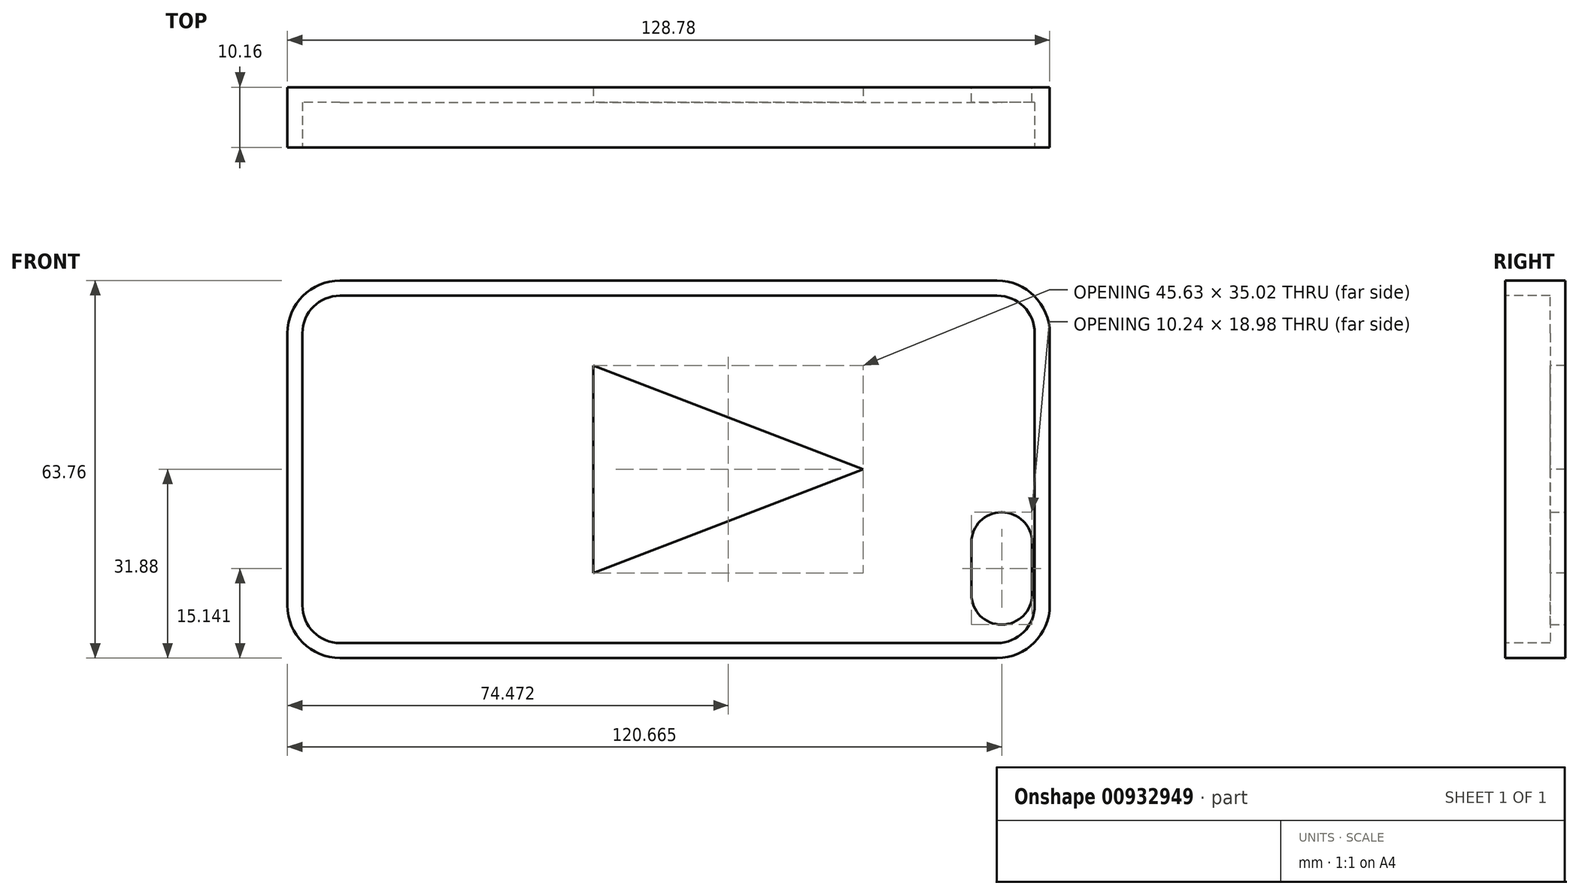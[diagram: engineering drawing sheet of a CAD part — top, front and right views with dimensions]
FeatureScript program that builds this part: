
annotation { "Feature Type Name" : "Feature", "Feature Type Description" : "" }
export const myFeature = defineFeature(function(context is Context, id is Id, definition is map)
    precondition{}
    {
        {
            var Q0;
            Q0=qCreatedBy(makeId("Front.planeOp"),FACE);
            var sketch = newSketch(context, id + "F0", { "sketchPlane" : qUnion([Q0])});
            skLineSegment(sketch, "E0.bottom", {"start": v(-55.5, 31.88) * mm, "end": v(55.5, 31.88) * mm});
            skLineSegment(sketch, "E0.top", {"start": v(-55.5, -31.88) * mm, "end": v(55.5, -31.88) * mm});
            skLineSegment(sketch, "E0.left", {"start": v(-64.39, 22.99) * mm, "end": v(-64.39, -22.99) * mm});
            skLineSegment(sketch, "E0.right", {"start": v(64.39, 22.99) * mm, "end": v(64.39, -22.99) * mm});
            skPoint(sketch, "E0.middle", {"position": v(0, 0) * mm});
            skPoint(sketch, "E1.visualSharp", {"position": v(-64.39, 31.88) * mm});
            skArc(sketch, "E1.filletArc", {"start": v(-55.5, 31.88) * mm, "mid": v(-61.79, 29.27) * mm, "end": v(-64.39, 22.99) * mm});
            skPoint(sketch, "E2.visualSharp", {"position": v(64.39, 31.88) * mm});
            skArc(sketch, "E2.filletArc", {"start": v(64.39, 22.99) * mm, "mid": v(61.79, 29.27) * mm, "end": v(55.5, 31.88) * mm});
            skPoint(sketch, "E3.visualSharp", {"position": v(64.39, -31.88) * mm});
            skArc(sketch, "E3.filletArc", {"start": v(55.5, -31.88) * mm, "mid": v(61.79, -29.27) * mm, "end": v(64.39, -22.99) * mm});
            skPoint(sketch, "E4.visualSharp", {"position": v(-64.39, -31.88) * mm});
            skArc(sketch, "E4.filletArc", {"start": v(-64.39, -22.99) * mm, "mid": v(-61.79, -29.27) * mm, "end": v(-55.5, -31.88) * mm});
            skSolve(sketch);
        }
        {
            var Q0;
            Q0=makeQuery(id+"F0.imprint","IMPRINT",FACE,{"disambiguationData":[TD([[makeQuery(id+"F0.imprint","IMPRINT",EDGE,{"derivedFrom":sQuery(id+"F0.wireOp",EDGE,"E0.bottom")}),-1.0]])]});
            extrude(context, id + "F1", {"entities" : qUnion([Q0]), "depth" : 10.16 * mm, "offsetDistance" : 25.4 * mm});
        }
        {
            var Q0;
            Q0=makeQuery(id+"F1.opExtrude","CAP_FACE",FACE,{"disambiguationData":[OSD([sQuery(id+"F0.wireOp",EDGE,"E0.bottom"),sQuery(id+"F0.wireOp",EDGE,"E0.top"),sQuery(id+"F0.wireOp",EDGE,"E0.left"),sQuery(id+"F0.wireOp",EDGE,"E0.right"),sQuery(id+"F0.wireOp",EDGE,"E1.filletArc"),sQuery(id+"F0.wireOp",EDGE,"E2.filletArc"),sQuery(id+"F0.wireOp",EDGE,"E3.filletArc"),sQuery(id+"F0.wireOp",EDGE,"E4.filletArc")])],"isStart":false});
            var sketch = newSketch(context, id + "F2", { "sketchPlane" : qUnion([Q0])});
            skLineSegment(sketch, "E5.bottom", {"start": v(-55.5, 29.34) * mm, "end": v(55.5, 29.34) * mm});
            skLineSegment(sketch, "E5.top", {"start": v(-55.5, -29.34) * mm, "end": v(55.5, -29.34) * mm});
            skLineSegment(sketch, "E5.left", {"start": v(-61.85, 22.99) * mm, "end": v(-61.85, -22.99) * mm});
            skLineSegment(sketch, "E5.right", {"start": v(61.85, 22.99) * mm, "end": v(61.85, -22.99) * mm});
            skPoint(sketch, "E5.middle", {"position": v(0, 0) * mm});
            skPoint(sketch, "E6.visualSharp", {"position": v(-61.85, 29.34) * mm});
            skArc(sketch, "E6.filletArc", {"start": v(-55.5, 29.34) * mm, "mid": v(-59.99, 27.48) * mm, "end": v(-61.85, 22.99) * mm});
            skPoint(sketch, "E7.visualSharp", {"position": v(61.85, 29.34) * mm});
            skArc(sketch, "E7.filletArc", {"start": v(61.85, 22.99) * mm, "mid": v(59.99, 27.48) * mm, "end": v(55.5, 29.34) * mm});
            skPoint(sketch, "E8.visualSharp", {"position": v(61.85, -29.34) * mm});
            skArc(sketch, "E8.filletArc", {"start": v(55.5, -29.34) * mm, "mid": v(59.99, -27.48) * mm, "end": v(61.85, -22.99) * mm});
            skPoint(sketch, "E9.visualSharp", {"position": v(-61.85, -29.34) * mm});
            skArc(sketch, "E9.filletArc", {"start": v(-61.85, -22.99) * mm, "mid": v(-59.99, -27.48) * mm, "end": v(-55.5, -29.34) * mm});
            skSolve(sketch);
        }
        {
            var Q0;
            Q0=makeQuery(id+"F2.imprint","IMPRINT",FACE,{"disambiguationData":[TD([[makeQuery(id+"F2.imprint","IMPRINT",EDGE,{"derivedFrom":sQuery(id+"F2.wireOp",EDGE,"E5.bottom")}),-1.0]])]});
            extrude(context, id + "F3", {"entities" : qUnion([Q0]), "operationType" : NewBodyOperationType.REMOVE, "oppositeDirection" : true, "depth" : 7.62 * mm, "offsetDistance" : 25.4 * mm});
        }
        {
            var Q0;
            Q0=makeQuery(id+"F1.opExtrude","CAP_FACE",FACE,{"disambiguationData":[OSD([sQuery(id+"F0.wireOp",EDGE,"E0.bottom"),sQuery(id+"F0.wireOp",EDGE,"E0.top"),sQuery(id+"F0.wireOp",EDGE,"E0.left"),sQuery(id+"F0.wireOp",EDGE,"E0.right"),sQuery(id+"F0.wireOp",EDGE,"E1.filletArc"),sQuery(id+"F0.wireOp",EDGE,"E2.filletArc"),sQuery(id+"F0.wireOp",EDGE,"E3.filletArc"),sQuery(id+"F0.wireOp",EDGE,"E4.filletArc")])],"isStart":true});
            var sketch = newSketch(context, id + "F4", { "sketchPlane" : qUnion([Q0])});
            skLineSegment(sketch, "E10.bottom", {"start": v(-56.31, -26.23) * mm, "end": v(-56.24, -26.23) * mm});
            skLineSegment(sketch, "E10.top", {"start": v(-56.31, -7.25) * mm, "end": v(-56.24, -7.25) * mm});
            skLineSegment(sketch, "E10.left", {"start": v(-61.4, -21.15) * mm, "end": v(-61.4, -12.33) * mm});
            skLineSegment(sketch, "E10.right", {"start": v(-51.16, -21.15) * mm, "end": v(-51.16, -12.33) * mm});
            skPoint(sketch, "E11.visualSharp", {"position": v(-61.4, -7.25) * mm});
            skArc(sketch, "E11.filletArc", {"start": v(-56.31, -7.25) * mm, "mid": v(-59.9, -8.74) * mm, "end": v(-61.4, -12.33) * mm});
            skPoint(sketch, "E12.visualSharp", {"position": v(-51.16, -26.23) * mm});
            skArc(sketch, "E12.filletArc", {"start": v(-56.24, -26.23) * mm, "mid": v(-52.64, -24.74) * mm, "end": v(-51.16, -21.15) * mm});
            skPoint(sketch, "E13.visualSharp", {"position": v(-51.16, -7.25) * mm});
            skArc(sketch, "E13.filletArc", {"start": v(-51.16, -12.33) * mm, "mid": v(-52.64, -8.74) * mm, "end": v(-56.24, -7.25) * mm});
            skPoint(sketch, "E14.visualSharp", {"position": v(-61.4, -26.23) * mm});
            skArc(sketch, "E14.filletArc", {"start": v(-61.4, -21.15) * mm, "mid": v(-59.9, -24.74) * mm, "end": v(-56.31, -26.23) * mm});
            skSolve(sketch);
        }
        {
            var Q0;
            Q0=qSketchRegion(id+"F4",true);
            extrude(context, id + "F5", {"entities" : qUnion([Q0]), "operationType" : NewBodyOperationType.REMOVE, "oppositeDirection" : true, "depth" : 25.4 * mm, "offsetDistance" : 25.4 * mm});
        }
        {
            var Q0;
            Q0=makeQuery(id+"F1.opExtrude","CAP_FACE",FACE,{"disambiguationData":[OSD([sQuery(id+"F0.wireOp",EDGE,"E0.bottom"),sQuery(id+"F0.wireOp",EDGE,"E0.top"),sQuery(id+"F0.wireOp",EDGE,"E0.left"),sQuery(id+"F0.wireOp",EDGE,"E0.right"),sQuery(id+"F0.wireOp",EDGE,"E1.filletArc"),sQuery(id+"F0.wireOp",EDGE,"E2.filletArc"),sQuery(id+"F0.wireOp",EDGE,"E3.filletArc"),sQuery(id+"F0.wireOp",EDGE,"E4.filletArc")])],"isStart":true});
            var sketch = newSketch(context, id + "F6", { "sketchPlane" : qUnion([Q0])});
            skLineSegment(sketch, "E15", {"start": v(-32.9, 0) * mm, "end": v(12.73, 17.51) * mm});
            skLineSegment(sketch, "E16.MirrorCS", {"start": v(-32.9, 0) * mm, "end": v(12.73, -17.51) * mm});
            skLineSegment(sketch, "E17", {"start": v(12.73, -17.51) * mm, "end": v(12.73, 17.51) * mm});
            skSolve(sketch);
        }
        {
            var Q0;
            Q0=makeQuery(id+"F6.imprint","IMPRINT",FACE,{"disambiguationData":[TD([[makeQuery(id+"F6.imprint","IMPRINT",EDGE,{"derivedFrom":sQuery(id+"F6.wireOp",EDGE,"E15")}),-1.0]])]});
            extrude(context, id + "F7", {"entities" : qUnion([Q0]), "operationType" : NewBodyOperationType.REMOVE, "depth" : 25.4 * mm, "offsetDistance" : 25.4 * mm, "hasSecondDirection" : true, "secondDirectionOppositeDirection" : true, "secondDirectionDepth" : 25.4 * mm});
        }
    });
